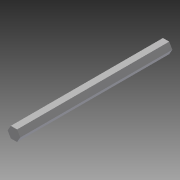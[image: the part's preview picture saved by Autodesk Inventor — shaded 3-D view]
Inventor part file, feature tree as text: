
AUTODESK INVENTOR PART (.ipt)
format: ipt  version: 2014 (Build 180170000, 170)  size: 74,752 bytes
history: native  units: in
note: dims shown in document units (in); Inventor stores cm internally (conversion verified against a paired STEP export)
features: plane x2, extrude x1, other x1, sketch x1
ambient origin geometry x8: Origin, YZ Plane, XZ Plane, XY Plane, X Axis, Y Axis, Z Axis, Center Point
bodies: Solid1 (feature_tree)
feature tree (5):
  extrude  "Extrusion1"  Depth=7.0in TaperAngle=0.0deg
  other  "Work Axis1"
  sketch  "Sketch1"  dims[d0=0.5in d1=7.0in d2=0.0in]
  plane  "Work Plane1"
  plane  "Work Plane2"
